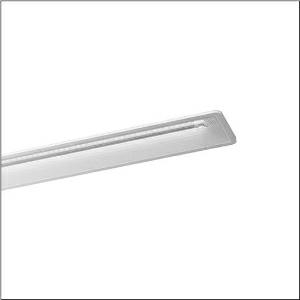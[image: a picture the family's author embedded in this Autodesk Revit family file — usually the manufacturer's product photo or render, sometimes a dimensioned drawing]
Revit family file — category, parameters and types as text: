
# Revit family: taris_r__21_5mt116704wd_f6c8
name_source: partatom
category: Lighting Fixtures
units: mm (PartAtom-declared; Revit-internal decimal feet)

## family parameters
Cut with Voids When Loaded = No
Host = Face
Light Source = No
Part Type = Normal
Room Calculation Point = No
Round Connector Dimension = Use Diameter
Shared = No

## types (1)
- Taris® 21 (1 x LED, 4910 lm, 30.6 W, 4000K)
    Apparent Load = 31 VA
    CIE Flux Codes = 73 96 99 100 100
    Color Rendering = 80
    Color Temperature = 4000K
    Default Elevation = 1800 mm
    Description = Taris® 21, office luminaire, primary anti-glare with micro louvre, primary optical cover: axial lens, of PMMA, structured, CAT 2 (L<= 1500cd/m²), light emission: direct distribution, primary light characteristic: symmetric, installation type: recessed, LED rated luminous flux: 4.910 lm, light colour: 840, colour temperature: 4000K, control gear: ECG, with terminal, 5-pole, mains connection: 230V, AC, 50Hz, rated input power: 31W, housing, luminaire housing, of plastic, traffic white (RAL 9016), module: M625, length: 1.250 mm, width: 150 mm, height: 76mm, recess depth: 106 mm, protection rating (complete): IP20, insulation class (complete): insulation class I (protective earthing), certification: CE, ENEC, VDE, protection symbol: F, impact resistance: IK02, permissible ambient temperature for indoor applications: 0..+35°C, standard: EN 50419, packaging unit: 1 piece
    Height = 0 mm  [stored 0 ft]
    Lamp = 1 x LED
    Lamp Light Flux = 4910 lm
    Lamp Power = 30.6 W
    Lamp count = 1
    Length = 1243 mm
    Luminous efficacy = 160 lm/W
    Manufacturer = Siteco
    ModVariant = No
    Model = 5MT116704WD
    Mounting Place = Ceiling
    Mounting Type = Recessed
    Number of Poles = 1
    OnlyDefault = Yes
    Power Factor = 1
    Product Name = Taris® 21
    Product group = office luminaire | ceiling recessed
    ProductGroupID = 400
    Protection Class = Protection class I
    Protection Degree = IP 20
    RLX_Detail_Level = 1
    RlxData = <blob elided: 26065 chars, md5=570e9553>
    Socket = socket
    Standby Power = 0 W
    System Light Flux = 4910 lm
    System Power = 31 W
    Type Comments = Product without accessories
    Type Image = l_1004723.jpg
    URL = http://relux.com
    VarID = ---
    Voltage = 0 V
    Weight = 0.00 kg
    Width = 144 mm

note: [stored X ft] marks values corroborated as IEEE doubles in the binary element streams (Revit-internal decimal feet)

## geometry (parser evidence)
native form markers: Blend x4, Sweep x11
no freeform markers — native parametric forms only
